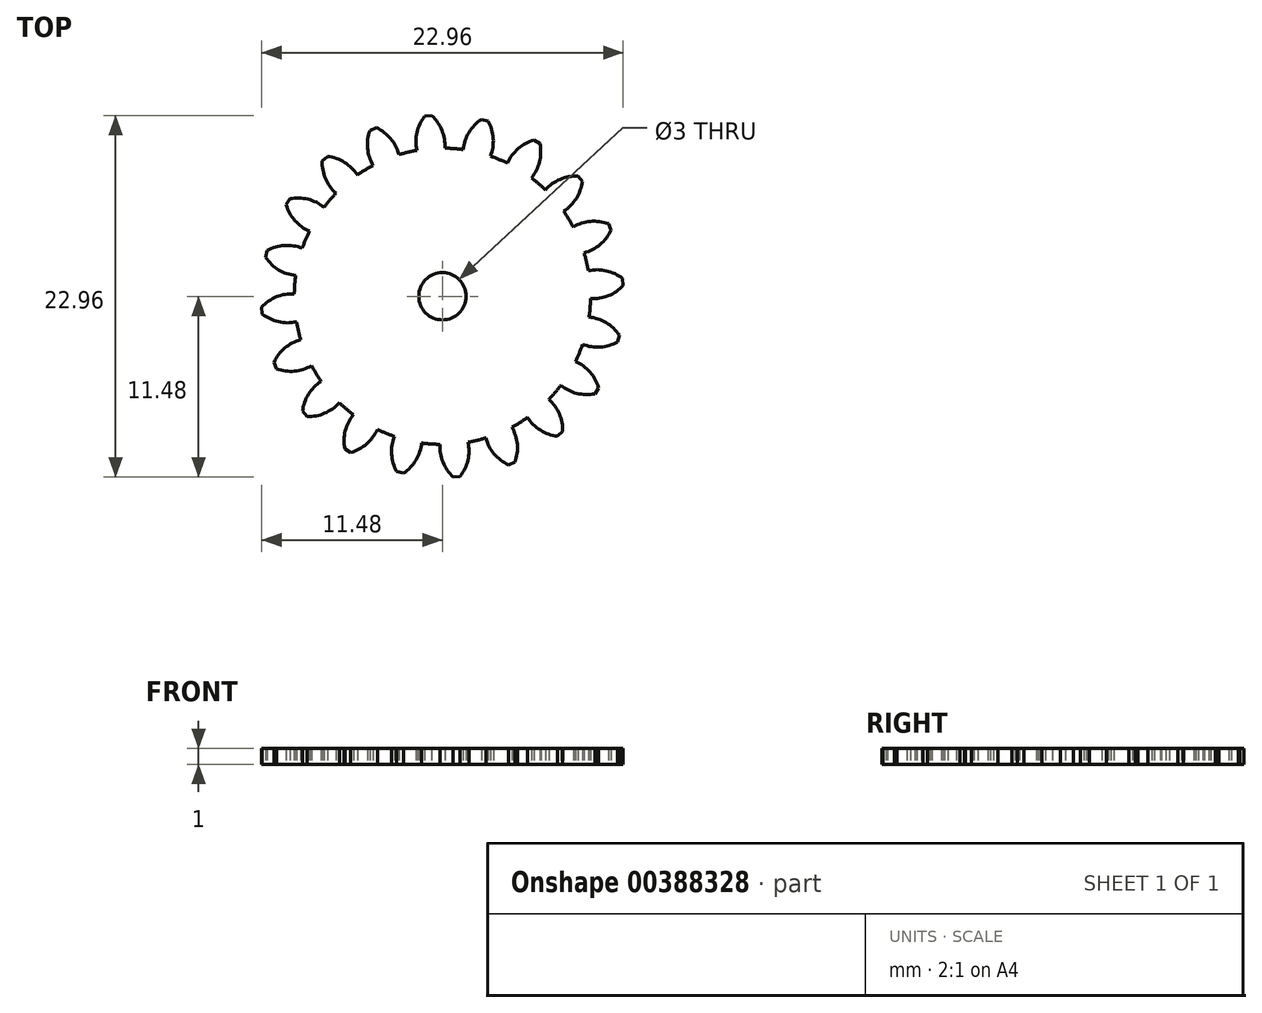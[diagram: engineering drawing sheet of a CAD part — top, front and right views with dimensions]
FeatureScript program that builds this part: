
annotation { "Feature Type Name" : "Feature", "Feature Type Description" : "" }
export const myFeature = defineFeature(function(context is Context, id is Id, definition is map)
    precondition{}
    {
        {
            assignVariable(context, id + "F0", {"name" : "GearDepth", "anyValue" : 1});
        }
        {
            var Q0;
            Q0=qCreatedBy(makeId("Top.planeOp"),FACE);
            var sketch = newSketch(context, id + "F1", { "sketchPlane" : qUnion([Q0])});
            skCircle(sketch, "E0", {"center": v(0, 0) * mm, "radius": 9.4 * mm});
            skCircle(sketch, "E1", {"center": v(0, 0) * mm, "radius": 10.45 * mm, "construction": true});
            skCircle(sketch, "E2", {"center": v(0, 0) * mm, "radius": 11.5 * mm, "construction": true});
            skLineSegment(sketch, "E3", {"start": v(0, 0) * mm, "end": v(0, 17.6) * mm, "construction": true});
            skLineSegment(sketch, "E4", {"start": v(0, 0) * mm, "end": v(-1.42, 18) * mm, "construction": true});
            skLineSegment(sketch, "E5", {"start": v(0, 10.45) * mm, "end": v(-10.54, 10.45) * mm, "construction": true});
            skLineSegment(sketch, "E6", {"start": v(0, 10.45) * mm, "end": v(-10.3, 6.7) * mm, "construction": true});
            skCircle(sketch, "E7", {"center": v(0, 10.45) * mm, "radius": 2.61 * mm, "construction": true});
            skCircle(sketch, "E8", {"center": v(-2.46, 9.56) * mm, "radius": 2.61 * mm, "construction": true});
            skArc(sketch, "E9", {"start": v(-4.91, 10.45) * mm, "mid": v(-4.92, 10.42) * mm, "end": v(-4.94, 10.39) * mm});
            skArc(sketch, "E10.trimOffspring", {"start": v(0.15, 9.4) * mm, "mid": v(-0.03, 10.54) * mm, "end": v(-0.68, 11.48) * mm});
            skArc(sketch, "E11.MirrorCS", {"start": v(-1.62, 9.27) * mm, "mid": v(-1.62, 10.41) * mm, "end": v(-1.12, 11.45) * mm});
            skLineSegment(sketch, "E12", {"start": v(-1.12, 11.45) * mm, "end": v(-0.68, 11.48) * mm});
            skArc(sketch, "E13.1.0", {"start": v(-2.76, 9) * mm, "mid": v(-3.29, 10.01) * mm, "end": v(-4.2, 10.7) * mm});
            skLineSegment(sketch, "E13.1.1", {"start": v(-4.6, 10.54) * mm, "end": v(-4.2, 10.7) * mm});
            skArc(sketch, "E13.1.2", {"start": v(-4.4, 8.31) * mm, "mid": v(-4.76, 9.4) * mm, "end": v(-4.6, 10.54) * mm});
            skArc(sketch, "E13.2.0", {"start": v(-5.4, 7.7) * mm, "mid": v(-6.22, 8.5) * mm, "end": v(-7.3, 8.89) * mm});
            skLineSegment(sketch, "E13.2.1", {"start": v(-7.64, 8.6) * mm, "end": v(-7.3, 8.89) * mm});
            skArc(sketch, "E13.2.2", {"start": v(-6.76, 6.54) * mm, "mid": v(-7.43, 7.47) * mm, "end": v(-7.64, 8.6) * mm});
            skArc(sketch, "E13.3.0", {"start": v(-7.52, 5.65) * mm, "mid": v(-8.54, 6.17) * mm, "end": v(-9.69, 6.2) * mm});
            skLineSegment(sketch, "E13.3.1", {"start": v(-9.92, 5.82) * mm, "end": v(-9.69, 6.2) * mm});
            skArc(sketch, "E13.3.2", {"start": v(-8.45, 4.13) * mm, "mid": v(-9.37, 4.81) * mm, "end": v(-9.92, 5.82) * mm});
            skArc(sketch, "E13.4.0", {"start": v(-8.9, 3.05) * mm, "mid": v(-10.03, 3.23) * mm, "end": v(-11.13, 2.9) * mm});
            skLineSegment(sketch, "E13.4.1", {"start": v(-11.23, 2.47) * mm, "end": v(-11.13, 2.9) * mm});
            skArc(sketch, "E13.4.2", {"start": v(-9.32, 1.32) * mm, "mid": v(-10.4, 1.68) * mm, "end": v(-11.23, 2.47) * mm});
            skArc(sketch, "E13.5.0", {"start": v(-9.4, 0.15) * mm, "mid": v(-10.54, -0.03) * mm, "end": v(-11.48, -0.68) * mm});
            skLineSegment(sketch, "E13.5.1", {"start": v(-11.45, -1.12) * mm, "end": v(-11.48, -0.68) * mm});
            skArc(sketch, "E13.5.2", {"start": v(-9.27, -1.62) * mm, "mid": v(-10.41, -1.62) * mm, "end": v(-11.45, -1.12) * mm});
            skArc(sketch, "E13.6.0", {"start": v(-9, -2.76) * mm, "mid": v(-10.01, -3.29) * mm, "end": v(-10.7, -4.2) * mm});
            skLineSegment(sketch, "E13.6.1", {"start": v(-10.54, -4.6) * mm, "end": v(-10.7, -4.2) * mm});
            skArc(sketch, "E13.6.2", {"start": v(-8.31, -4.4) * mm, "mid": v(-9.4, -4.76) * mm, "end": v(-10.54, -4.6) * mm});
            skArc(sketch, "E13.7.0", {"start": v(-7.7, -5.4) * mm, "mid": v(-8.5, -6.22) * mm, "end": v(-8.89, -7.3) * mm});
            skLineSegment(sketch, "E13.7.1", {"start": v(-8.6, -7.64) * mm, "end": v(-8.89, -7.3) * mm});
            skArc(sketch, "E13.7.2", {"start": v(-6.54, -6.76) * mm, "mid": v(-7.47, -7.43) * mm, "end": v(-8.6, -7.64) * mm});
            skArc(sketch, "E13.8.0", {"start": v(-5.65, -7.52) * mm, "mid": v(-6.17, -8.54) * mm, "end": v(-6.2, -9.69) * mm});
            skLineSegment(sketch, "E13.8.1", {"start": v(-5.82, -9.92) * mm, "end": v(-6.2, -9.69) * mm});
            skArc(sketch, "E13.8.2", {"start": v(-4.13, -8.45) * mm, "mid": v(-4.81, -9.37) * mm, "end": v(-5.82, -9.92) * mm});
            skArc(sketch, "E13.9.0", {"start": v(-3.05, -8.9) * mm, "mid": v(-3.23, -10.03) * mm, "end": v(-2.9, -11.13) * mm});
            skLineSegment(sketch, "E13.9.1", {"start": v(-2.47, -11.23) * mm, "end": v(-2.9, -11.13) * mm});
            skArc(sketch, "E13.9.2", {"start": v(-1.32, -9.32) * mm, "mid": v(-1.68, -10.4) * mm, "end": v(-2.47, -11.23) * mm});
            skArc(sketch, "E13.10.0", {"start": v(-0.15, -9.4) * mm, "mid": v(0.03, -10.54) * mm, "end": v(0.68, -11.48) * mm});
            skLineSegment(sketch, "E13.10.1", {"start": v(1.12, -11.45) * mm, "end": v(0.68, -11.48) * mm});
            skArc(sketch, "E13.10.2", {"start": v(1.62, -9.27) * mm, "mid": v(1.62, -10.41) * mm, "end": v(1.12, -11.45) * mm});
            skArc(sketch, "E13.11.0", {"start": v(2.76, -9) * mm, "mid": v(3.29, -10.01) * mm, "end": v(4.2, -10.7) * mm});
            skLineSegment(sketch, "E13.11.1", {"start": v(4.6, -10.54) * mm, "end": v(4.2, -10.7) * mm});
            skArc(sketch, "E13.11.2", {"start": v(4.4, -8.31) * mm, "mid": v(4.76, -9.4) * mm, "end": v(4.6, -10.54) * mm});
            skArc(sketch, "E13.12.0", {"start": v(5.4, -7.7) * mm, "mid": v(6.22, -8.5) * mm, "end": v(7.3, -8.89) * mm});
            skLineSegment(sketch, "E13.12.1", {"start": v(7.64, -8.6) * mm, "end": v(7.3, -8.89) * mm});
            skArc(sketch, "E13.12.2", {"start": v(6.76, -6.54) * mm, "mid": v(7.43, -7.47) * mm, "end": v(7.64, -8.6) * mm});
            skArc(sketch, "E13.13.0", {"start": v(7.52, -5.65) * mm, "mid": v(8.54, -6.17) * mm, "end": v(9.69, -6.2) * mm});
            skLineSegment(sketch, "E13.13.1", {"start": v(9.92, -5.82) * mm, "end": v(9.69, -6.2) * mm});
            skArc(sketch, "E13.13.2", {"start": v(8.45, -4.13) * mm, "mid": v(9.37, -4.81) * mm, "end": v(9.92, -5.82) * mm});
            skArc(sketch, "E13.14.0", {"start": v(8.9, -3.05) * mm, "mid": v(10.03, -3.23) * mm, "end": v(11.13, -2.9) * mm});
            skLineSegment(sketch, "E13.14.1", {"start": v(11.23, -2.47) * mm, "end": v(11.13, -2.9) * mm});
            skArc(sketch, "E13.14.2", {"start": v(9.32, -1.32) * mm, "mid": v(10.4, -1.68) * mm, "end": v(11.23, -2.47) * mm});
            skArc(sketch, "E13.15.0", {"start": v(9.4, -0.15) * mm, "mid": v(10.54, 0.03) * mm, "end": v(11.48, 0.68) * mm});
            skLineSegment(sketch, "E13.15.1", {"start": v(11.45, 1.12) * mm, "end": v(11.48, 0.68) * mm});
            skArc(sketch, "E13.15.2", {"start": v(9.27, 1.62) * mm, "mid": v(10.41, 1.62) * mm, "end": v(11.45, 1.12) * mm});
            skArc(sketch, "E13.16.0", {"start": v(9, 2.76) * mm, "mid": v(10.01, 3.29) * mm, "end": v(10.7, 4.2) * mm});
            skLineSegment(sketch, "E13.16.1", {"start": v(10.54, 4.6) * mm, "end": v(10.7, 4.2) * mm});
            skArc(sketch, "E13.16.2", {"start": v(8.31, 4.4) * mm, "mid": v(9.4, 4.76) * mm, "end": v(10.54, 4.6) * mm});
            skArc(sketch, "E13.17.0", {"start": v(7.7, 5.4) * mm, "mid": v(8.5, 6.22) * mm, "end": v(8.89, 7.3) * mm});
            skLineSegment(sketch, "E13.17.1", {"start": v(8.6, 7.64) * mm, "end": v(8.89, 7.3) * mm});
            skArc(sketch, "E13.17.2", {"start": v(6.54, 6.76) * mm, "mid": v(7.47, 7.43) * mm, "end": v(8.6, 7.64) * mm});
            skArc(sketch, "E13.18.0", {"start": v(5.65, 7.52) * mm, "mid": v(6.17, 8.54) * mm, "end": v(6.2, 9.69) * mm});
            skLineSegment(sketch, "E13.18.1", {"start": v(5.82, 9.92) * mm, "end": v(6.2, 9.69) * mm});
            skArc(sketch, "E13.18.2", {"start": v(4.13, 8.45) * mm, "mid": v(4.81, 9.37) * mm, "end": v(5.82, 9.92) * mm});
            skArc(sketch, "E13.19.0", {"start": v(3.05, 8.9) * mm, "mid": v(3.23, 10.03) * mm, "end": v(2.9, 11.13) * mm});
            skLineSegment(sketch, "E13.19.1", {"start": v(2.47, 11.23) * mm, "end": v(2.9, 11.13) * mm});
            skArc(sketch, "E13.19.2", {"start": v(1.32, 9.32) * mm, "mid": v(1.68, 10.4) * mm, "end": v(2.47, 11.23) * mm});
            skCircle(sketch, "E14", {"center": v(0, 0) * mm, "radius": 1.5 * mm});
            skSolve(sketch);
        }
        {
            var Q0;
            {var subQ0=sQuery(id+"F1.wireOp",EDGE,"E10.trimOffspring");Q0=makeQuery(id+"F1.imprint","IMPRINT",FACE,{"disambiguationData":[TD([[makeQuery(id+"F1.imprint","IMPRINT",EDGE,{"derivedFrom":subQ0}),1.0]])]});}
            var Q1;
            {var subQ0=sQuery(id+"F1.wireOp",EDGE,"E0");var subQ1=makeQuery(id+"F1.imprint","INTERSECT",VERTEX,{"derivedFrom":[subQ0,sQuery(id+"F1.wireOp",EDGE,"E10.trimOffspring")]});Q1=makeQuery(id+"F1.imprint","IMPRINT",FACE,{"disambiguationData":[TD([[makeQuery(id+"F1.imprint","IMPRINT",EDGE,{"disambiguationData":[TD([[subQ1,-1.0]])],"derivedFrom":subQ0}),1.0]])]});}
            var Q2;
            {var subQ0=sQuery(id+"F1.wireOp",EDGE,"E13.1.0");Q2=makeQuery(id+"F1.imprint","IMPRINT",FACE,{"disambiguationData":[TD([[makeQuery(id+"F1.imprint","IMPRINT",EDGE,{"derivedFrom":subQ0}),1.0]])]});}
            var Q3;
            {var subQ0=sQuery(id+"F1.wireOp",EDGE,"E13.2.0");Q3=makeQuery(id+"F1.imprint","IMPRINT",FACE,{"disambiguationData":[TD([[makeQuery(id+"F1.imprint","IMPRINT",EDGE,{"derivedFrom":subQ0}),1.0]])]});}
            var Q4;
            {var subQ0=sQuery(id+"F1.wireOp",EDGE,"E13.3.0");Q4=makeQuery(id+"F1.imprint","IMPRINT",FACE,{"disambiguationData":[TD([[makeQuery(id+"F1.imprint","IMPRINT",EDGE,{"derivedFrom":subQ0}),1.0]])]});}
            var Q5;
            {var subQ0=sQuery(id+"F1.wireOp",EDGE,"E13.4.0");Q5=makeQuery(id+"F1.imprint","IMPRINT",FACE,{"disambiguationData":[TD([[makeQuery(id+"F1.imprint","IMPRINT",EDGE,{"derivedFrom":subQ0}),1.0]])]});}
            var Q6;
            {var subQ0=sQuery(id+"F1.wireOp",EDGE,"E13.5.0");Q6=makeQuery(id+"F1.imprint","IMPRINT",FACE,{"disambiguationData":[TD([[makeQuery(id+"F1.imprint","IMPRINT",EDGE,{"derivedFrom":subQ0}),1.0]])]});}
            var Q7;
            {var subQ0=sQuery(id+"F1.wireOp",EDGE,"E13.6.0");Q7=makeQuery(id+"F1.imprint","IMPRINT",FACE,{"disambiguationData":[TD([[makeQuery(id+"F1.imprint","IMPRINT",EDGE,{"derivedFrom":subQ0}),1.0]])]});}
            var Q8;
            {var subQ0=sQuery(id+"F1.wireOp",EDGE,"E13.7.0");Q8=makeQuery(id+"F1.imprint","IMPRINT",FACE,{"disambiguationData":[TD([[makeQuery(id+"F1.imprint","IMPRINT",EDGE,{"derivedFrom":subQ0}),1.0]])]});}
            var Q9;
            {var subQ0=sQuery(id+"F1.wireOp",EDGE,"E13.8.0");Q9=makeQuery(id+"F1.imprint","IMPRINT",FACE,{"disambiguationData":[TD([[makeQuery(id+"F1.imprint","IMPRINT",EDGE,{"derivedFrom":subQ0}),1.0]])]});}
            var Q10;
            {var subQ0=sQuery(id+"F1.wireOp",EDGE,"E13.9.0");Q10=makeQuery(id+"F1.imprint","IMPRINT",FACE,{"disambiguationData":[TD([[makeQuery(id+"F1.imprint","IMPRINT",EDGE,{"derivedFrom":subQ0}),1.0]])]});}
            var Q11;
            {var subQ0=sQuery(id+"F1.wireOp",EDGE,"E13.10.0");Q11=makeQuery(id+"F1.imprint","IMPRINT",FACE,{"disambiguationData":[TD([[makeQuery(id+"F1.imprint","IMPRINT",EDGE,{"derivedFrom":subQ0}),1.0]])]});}
            var Q12;
            {var subQ0=sQuery(id+"F1.wireOp",EDGE,"E13.11.0");Q12=makeQuery(id+"F1.imprint","IMPRINT",FACE,{"disambiguationData":[TD([[makeQuery(id+"F1.imprint","IMPRINT",EDGE,{"derivedFrom":subQ0}),1.0]])]});}
            var Q13;
            {var subQ0=sQuery(id+"F1.wireOp",EDGE,"E13.12.0");Q13=makeQuery(id+"F1.imprint","IMPRINT",FACE,{"disambiguationData":[TD([[makeQuery(id+"F1.imprint","IMPRINT",EDGE,{"derivedFrom":subQ0}),1.0]])]});}
            var Q14;
            {var subQ0=sQuery(id+"F1.wireOp",EDGE,"E13.13.0");Q14=makeQuery(id+"F1.imprint","IMPRINT",FACE,{"disambiguationData":[TD([[makeQuery(id+"F1.imprint","IMPRINT",EDGE,{"derivedFrom":subQ0}),1.0]])]});}
            var Q15;
            {var subQ0=sQuery(id+"F1.wireOp",EDGE,"E13.14.0");Q15=makeQuery(id+"F1.imprint","IMPRINT",FACE,{"disambiguationData":[TD([[makeQuery(id+"F1.imprint","IMPRINT",EDGE,{"derivedFrom":subQ0}),1.0]])]});}
            var Q16;
            {var subQ0=sQuery(id+"F1.wireOp",EDGE,"E13.15.0");Q16=makeQuery(id+"F1.imprint","IMPRINT",FACE,{"disambiguationData":[TD([[makeQuery(id+"F1.imprint","IMPRINT",EDGE,{"derivedFrom":subQ0}),1.0]])]});}
            var Q17;
            {var subQ0=sQuery(id+"F1.wireOp",EDGE,"E13.16.0");Q17=makeQuery(id+"F1.imprint","IMPRINT",FACE,{"disambiguationData":[TD([[makeQuery(id+"F1.imprint","IMPRINT",EDGE,{"derivedFrom":subQ0}),1.0]])]});}
            var Q18;
            {var subQ0=sQuery(id+"F1.wireOp",EDGE,"E13.17.0");Q18=makeQuery(id+"F1.imprint","IMPRINT",FACE,{"disambiguationData":[TD([[makeQuery(id+"F1.imprint","IMPRINT",EDGE,{"derivedFrom":subQ0}),1.0]])]});}
            var Q19;
            {var subQ0=sQuery(id+"F1.wireOp",EDGE,"E13.18.0");Q19=makeQuery(id+"F1.imprint","IMPRINT",FACE,{"disambiguationData":[TD([[makeQuery(id+"F1.imprint","IMPRINT",EDGE,{"derivedFrom":subQ0}),1.0]])]});}
            var Q20;
            {var subQ0=sQuery(id+"F1.wireOp",EDGE,"E13.19.0");Q20=makeQuery(id+"F1.imprint","IMPRINT",FACE,{"disambiguationData":[TD([[makeQuery(id+"F1.imprint","IMPRINT",EDGE,{"derivedFrom":subQ0}),1.0]])]});}
            var Q21;
            Q21=sQuery(id+"F1.wireOp",EDGE,"E0");
            var Q22;
            Q22=sQuery(id+"F1.wireOp",EDGE,"E10.trimOffspring");
            var Q23;
            Q23=sQuery(id+"F1.wireOp",EDGE,"E12");
            var Q24;
            Q24=sQuery(id+"F1.wireOp",EDGE,"E11.MirrorCS");
            extrude(context, id + "F2", {"entities" : qUnion([Q0, Q1, Q2, Q3, Q4, Q5, Q6, Q7, Q8, Q9, Q10, Q11, Q12, Q13, Q14, Q15, Q16, Q17, Q18, Q19, Q20]), "surfaceEntities" : qUnion([Q21, Q22, Q23, Q24]), "depth" : (getVariable(context, 'GearDepth')) * mm});
        }
    });
